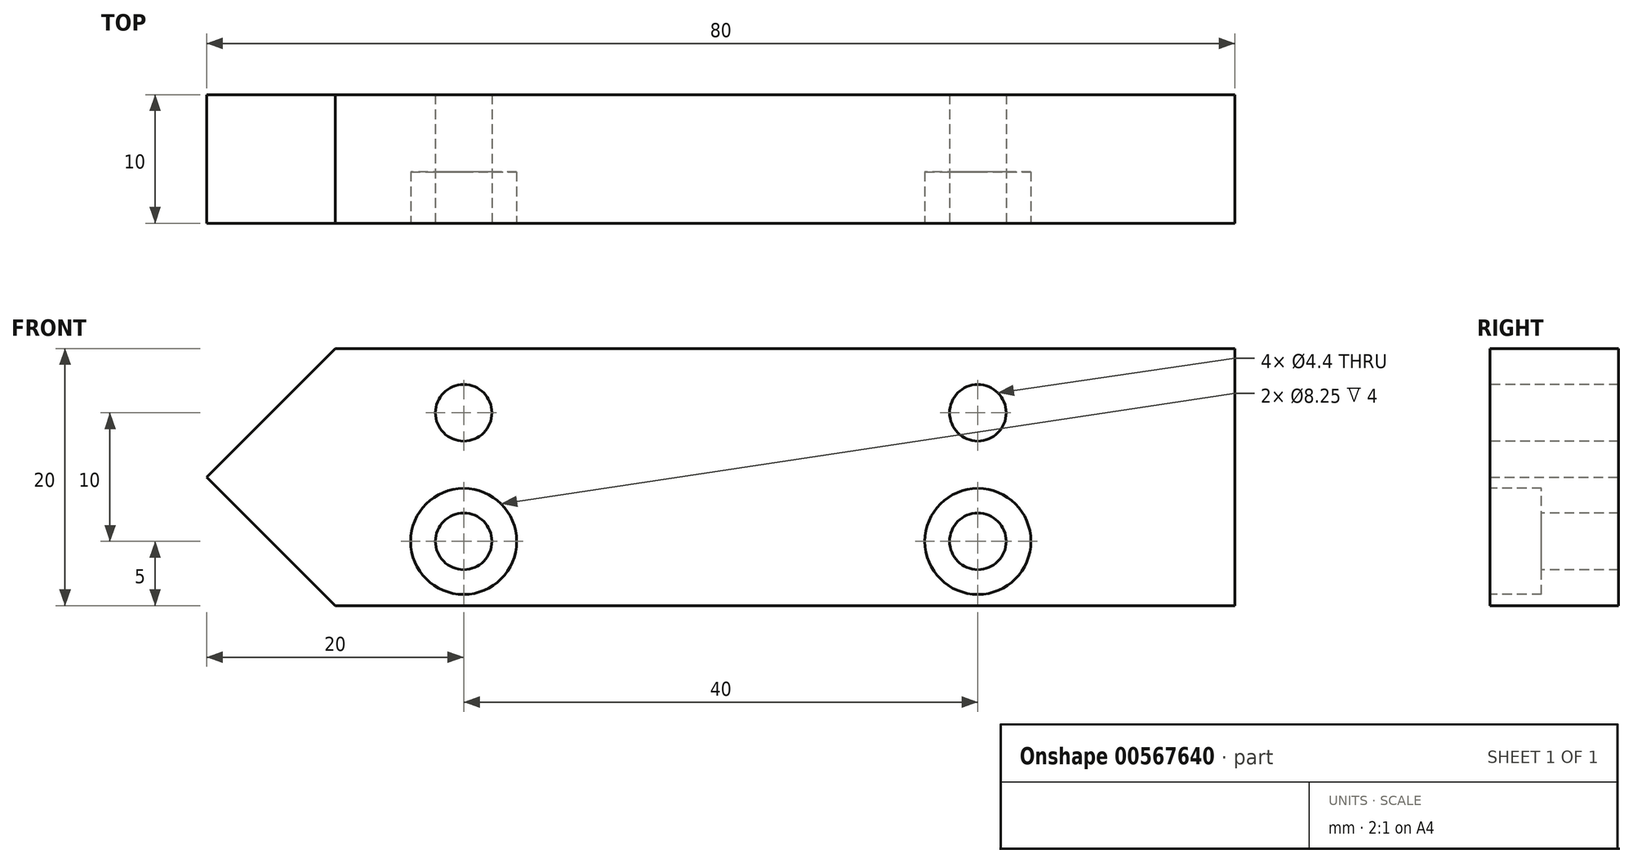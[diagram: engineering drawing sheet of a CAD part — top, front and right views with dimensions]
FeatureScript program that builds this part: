
annotation { "Feature Type Name" : "Feature", "Feature Type Description" : "" }
export const myFeature = defineFeature(function(context is Context, id is Id, definition is map)
    precondition{}
    {
        {
            var Q0;
            Q0=qCreatedBy(makeId("Front.planeOp"),FACE);
            var sketch = newSketch(context, id + "F0", { "sketchPlane" : qUnion([Q0])});
            skLineSegment(sketch, "E0", {"start": v(0, 0) * mm, "end": v(-70, 0) * mm});
            skLineSegment(sketch, "E1", {"start": v(0, 0) * mm, "end": v(0, 20) * mm});
            skLineSegment(sketch, "E2", {"start": v(0, 20) * mm, "end": v(-70, 20) * mm});
            skLineSegment(sketch, "E3", {"start": v(0, 10) * mm, "end": v(-80, 10) * mm});
            skPoint(sketch, "E3.endSnap0", {"position": v(0, 10) * mm});
            skLineSegment(sketch, "E4", {"start": v(-70, 0) * mm, "end": v(-80, 10) * mm});
            skLineSegment(sketch, "E5", {"start": v(-80, 10) * mm, "end": v(-70, 20) * mm});
            skSolve(sketch);
        }
        {
            var Q0;
            Q0=makeQuery(id+"F0.imprint","IMPRINT",FACE,{"disambiguationData":[TD([[makeQuery(id+"F0.imprint","IMPRINT",EDGE,{"derivedFrom":sQuery(id+"F0.wireOp",EDGE,"mtNnAYYq-jTvC-UR4u-BWhf-MOKAIkZ2tAMb.bottom")}),1.0]])]});
            var Q1;
            {var subQ0=sQuery(id+"F0.wireOp",EDGE,"E2");Q1=makeQuery(id+"F0.imprint","IMPRINT",FACE,{"disambiguationData":[TD([[makeQuery(id+"F0.imprint","IMPRINT",EDGE,{"derivedFrom":subQ0}),1.0]])]});}
            var Q2;
            {var subQ0=sQuery(id+"F0.wireOp",EDGE,"E0");Q2=makeQuery(id+"F0.imprint","IMPRINT",FACE,{"disambiguationData":[TD([[makeQuery(id+"F0.imprint","IMPRINT",EDGE,{"derivedFrom":subQ0}),-1.0]])]});}
            extrude(context, id + "F1", {"entities" : qUnion([Q0, Q1, Q2]), "depth" : 10 * mm, "offsetDistance" : 25 * mm});
        }
        {
            var Q0;
            Q0=makeQuery(id+"F1.opExtrude","CAP_FACE",FACE,{"disambiguationData":[OSD([sQuery(id+"F0.wireOp",EDGE,"E0"),sQuery(id+"F0.wireOp",EDGE,"E1"),sQuery(id+"F0.wireOp",EDGE,"E2"),sQuery(id+"F0.wireOp",EDGE,"E4"),sQuery(id+"F0.wireOp",EDGE,"E5")])],"isStart":false});
            var sketch = newSketch(context, id + "F2", { "sketchPlane" : qUnion([Q0])});
            skLineSegment(sketch, "E6", {"start": v(-60, 0) * mm, "end": v(-60, 5) * mm});
            skLineSegment(sketch, "E7", {"start": v(-20, 0) * mm, "end": v(-20, 5) * mm});
            skSolve(sketch);
        }
        {
            var Q0;
            Q0=sQuery(id+"F2.wireOp",VERTEX,"E7.end");
            var Q1;
            Q1=sQuery(id+"F2.wireOp",VERTEX,"E6.end");
            var Q2;
            Q2=makeQuery(id+"F1.opExtrude","SWEPT_BODY",BODY,{"disambiguationData":[OSD([sQuery(id+"F0.wireOp",EDGE,"E0"),sQuery(id+"F0.wireOp",EDGE,"E1"),sQuery(id+"F0.wireOp",EDGE,"E2"),sQuery(id+"F0.wireOp",EDGE,"E4"),sQuery(id+"F0.wireOp",EDGE,"E5")])]});
            hole(context, id + "F3", {"style" : HoleStyle.C_BORE, "endStyle" : HoleEndStyle.THROUGH, "standardTappedOrClearance" : lookupTablePath({ "standard" : "ISO", "fit" : "Normal", "size" : "M4", "type" : "Clearance" }), "standardBlindInLast" : lookupTablePath({ "fit" : "Standard", "standard" : "ISO", "size" : "M4", "type" : "Clearance" }), "holeDiameter" : 4.4 * mm, "cBoreDiameter" : 8.25 * mm, "cBoreDepth" : 4 * mm, "isTappedThrough" : true, "tappedDepth" : 12 * mm, "tapClearance" : 3, "locations" : qUnion([Q0, Q1]), "scope" : qUnion([Q2])});
        }
        {
            var Q0;
            Q0=makeQuery(id+"F1.opExtrude","CAP_FACE",FACE,{"disambiguationData":[OSD([sQuery(id+"F0.wireOp",EDGE,"E0"),sQuery(id+"F0.wireOp",EDGE,"E1"),sQuery(id+"F0.wireOp",EDGE,"E2"),sQuery(id+"F0.wireOp",EDGE,"E4"),sQuery(id+"F0.wireOp",EDGE,"E5")])],"isStart":false});
            var sketch = newSketch(context, id + "F4", { "sketchPlane" : qUnion([Q0])});
            skLineSegment(sketch, "E8", {"start": v(-60, 20) * mm, "end": v(-60, 15) * mm});
            skLineSegment(sketch, "E9", {"start": v(-20, 20) * mm, "end": v(-20, 15) * mm});
            skSolve(sketch);
        }
        {
            var Q0;
            Q0=sQuery(id+"F4.wireOp",VERTEX,"E8.end");
            var Q1;
            Q1=sQuery(id+"F4.wireOp",VERTEX,"E9.end");
            var Q2;
            Q2=makeQuery(id+"F1.opExtrude","SWEPT_BODY",BODY,{"disambiguationData":[OSD([sQuery(id+"F0.wireOp",EDGE,"E0"),sQuery(id+"F0.wireOp",EDGE,"E1"),sQuery(id+"F0.wireOp",EDGE,"E2"),sQuery(id+"F0.wireOp",EDGE,"E4"),sQuery(id+"F0.wireOp",EDGE,"E5")])]});
            hole(context, id + "F5", {"style" : HoleStyle.SIMPLE, "endStyle" : HoleEndStyle.THROUGH, "standardTappedOrClearance" : lookupTablePath({ "standard" : "ISO", "fit" : "Normal", "size" : "M4", "type" : "Clearance" }), "standardBlindInLast" : lookupTablePath({ "fit" : "Standard", "standard" : "ISO", "size" : "M4", "type" : "Clearance" }), "holeDiameter" : 4.4 * mm, "isTappedThrough" : true, "tappedDepth" : 12 * mm, "tapClearance" : 3, "locations" : qUnion([Q0, Q1]), "scope" : qUnion([Q2])});
        }
    });
